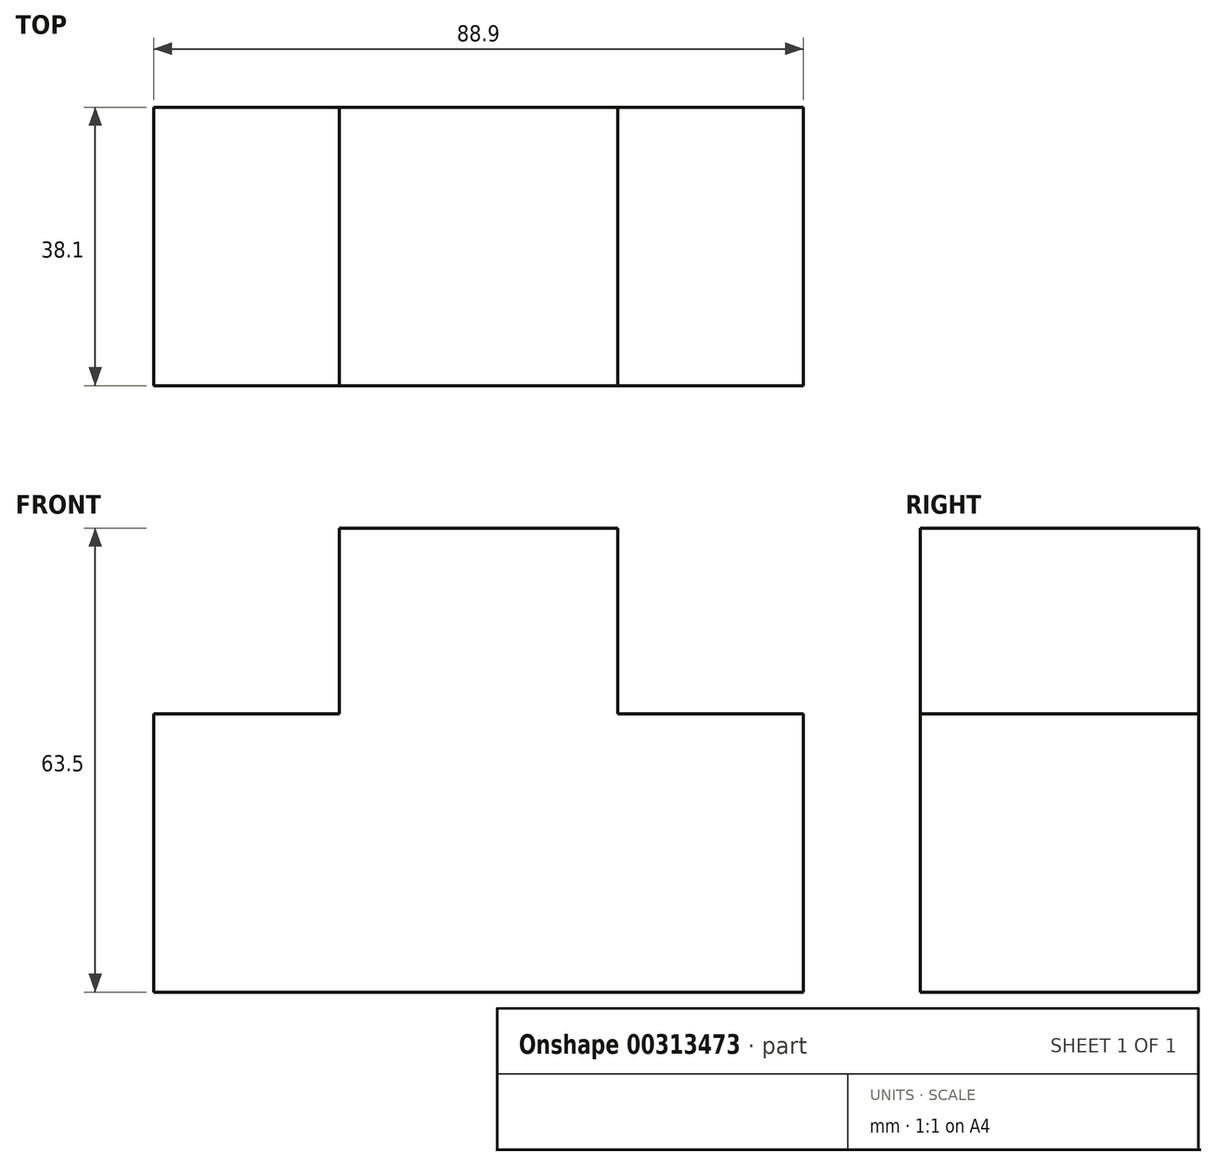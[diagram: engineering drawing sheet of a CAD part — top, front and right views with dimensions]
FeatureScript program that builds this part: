
annotation { "Feature Type Name" : "Feature", "Feature Type Description" : "" }
export const myFeature = defineFeature(function(context is Context, id is Id, definition is map)
    precondition{}
    {
        {
            var Q0;
            Q0=qCreatedBy(makeId("Front.planeOp"),FACE);
            var sketch = newSketch(context, id + "F0", { "sketchPlane" : qUnion([Q0])});
            skLineSegment(sketch, "E0", {"start": v(-53.27, -41.27) * mm, "end": v(35.63, -41.27) * mm});
            skLineSegment(sketch, "E1", {"start": v(-53.27, -41.27) * mm, "end": v(-53.27, -3.17) * mm});
            skLineSegment(sketch, "E2", {"start": v(-53.27, -3.17) * mm, "end": v(-27.87, -3.17) * mm});
            skLineSegment(sketch, "E3", {"start": v(-27.87, -3.17) * mm, "end": v(-27.87, 22.23) * mm});
            skLineSegment(sketch, "E4", {"start": v(-27.87, 22.23) * mm, "end": v(10.23, 22.23) * mm});
            skLineSegment(sketch, "E5", {"start": v(10.23, 22.23) * mm, "end": v(10.23, -3.17) * mm});
            skLineSegment(sketch, "E6", {"start": v(10.23, -3.17) * mm, "end": v(35.63, -3.17) * mm});
            skLineSegment(sketch, "E7", {"start": v(35.63, -3.17) * mm, "end": v(35.63, -41.27) * mm});
            skSolve(sketch);
        }
        {
            var Q0;
            Q0=makeQuery(id+"F0.imprint","IMPRINT",FACE,{"disambiguationData":[TD([[makeQuery(id+"F0.imprint","IMPRINT",EDGE,{"derivedFrom":sQuery(id+"F0.wireOp",EDGE,"E0")}),1.0]])]});
            extrude(context, id + "F1", {"entities" : qUnion([Q0]), "depth" : 38.1 * mm});
        }
    });
